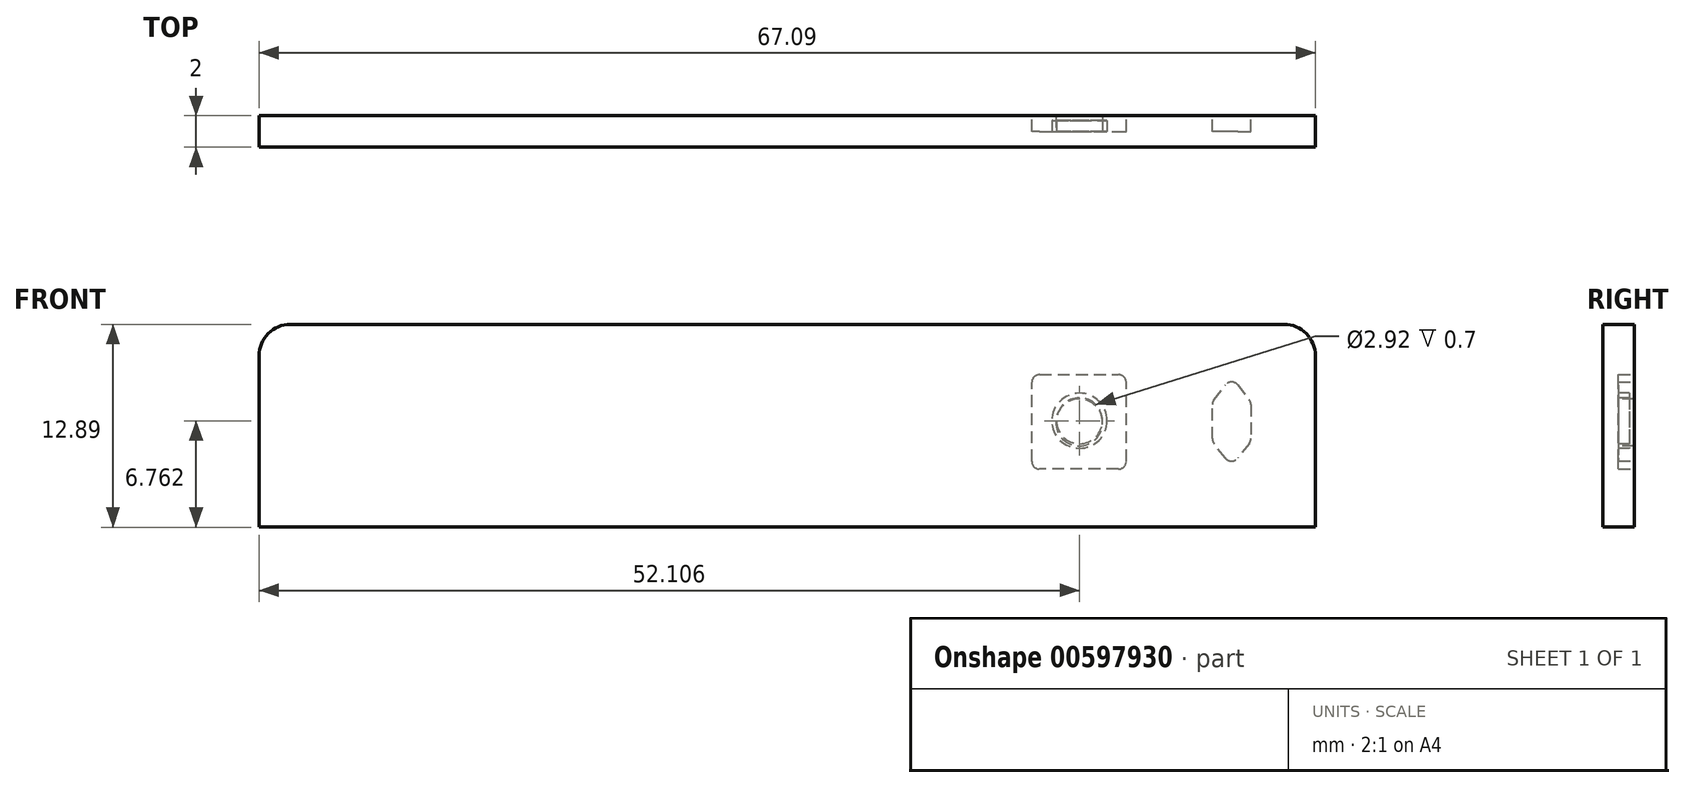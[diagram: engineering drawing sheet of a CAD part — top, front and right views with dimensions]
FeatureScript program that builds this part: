
annotation { "Feature Type Name" : "Feature", "Feature Type Description" : "" }
export const myFeature = defineFeature(function(context is Context, id is Id, definition is map)
    precondition{}
    {
        {
            var Q0;
            Q0=qCreatedBy(makeId("Front.planeOp"),FACE);
            var sketch = newSketch(context, id + "F0", { "sketchPlane" : qUnion([Q0])});
            skLineSegment(sketch, "E0", {"start": v(-68, 133.08) * mm, "end": v(-0.9, 133.08) * mm});
            skLineSegment(sketch, "E1", {"start": v(-0.9, 133.08) * mm, "end": v(-0.9, 143.97) * mm});
            skLineSegment(sketch, "E2", {"start": v(-2.9, 145.97) * mm, "end": v(-66, 145.97) * mm});
            skLineSegment(sketch, "E3", {"start": v(-68, 143.97) * mm, "end": v(-68, 133.08) * mm});
            skPoint(sketch, "E4.visualSharp", {"position": v(-0.9, 145.97) * mm});
            skArc(sketch, "E4.filletArc", {"start": v(-0.9, 143.97) * mm, "mid": v(-1.49, 145.38) * mm, "end": v(-2.9, 145.97) * mm});
            skPoint(sketch, "E5.visualSharp", {"position": v(-68, 145.97) * mm});
            skArc(sketch, "E5.filletArc", {"start": v(-66, 145.97) * mm, "mid": v(-67.4, 145.38) * mm, "end": v(-68, 143.97) * mm});
            skSolve(sketch);
        }
        {
            var Q0;
            Q0=makeQuery(id+"F0.imprint","IMPRINT",FACE,{"disambiguationData":[TD([[makeQuery(id+"F0.imprint","IMPRINT",EDGE,{"derivedFrom":sQuery(id+"F0.wireOp",EDGE,"E0")}),1.0]])]});
            extrude(context, id + "F1", {"entities" : qUnion([Q0]), "oppositeDirection" : true, "depth" : 2 * mm, "offsetDistance" : 25 * mm});
        }
        {
            var Q0;
            Q0=makeQuery(id+"F1.opExtrude","CAP_FACE",FACE,{"disambiguationData":[OSD([sQuery(id+"F0.wireOp",EDGE,"E0"),sQuery(id+"F0.wireOp",EDGE,"E1"),sQuery(id+"F0.wireOp",EDGE,"E2"),sQuery(id+"F0.wireOp",EDGE,"E3"),sQuery(id+"F0.wireOp",EDGE,"E4.filletArc"),sQuery(id+"F0.wireOp",EDGE,"E5.filletArc")])],"isStart":false});
            var sketch = newSketch(context, id + "F2", { "sketchPlane" : qUnion([Q0])});
            skLineSegment(sketch, "E6", {"start": v(13.41, 136.77) * mm, "end": v(18.41, 136.77) * mm});
            skLineSegment(sketch, "E7", {"start": v(18.91, 137.27) * mm, "end": v(18.91, 142.27) * mm});
            skLineSegment(sketch, "E8", {"start": v(18.41, 142.77) * mm, "end": v(13.41, 142.77) * mm});
            skPoint(sketch, "E9.visualSharp", {"position": v(18.91, 142.77) * mm});
            skArc(sketch, "E9.filletArc", {"start": v(18.91, 142.27) * mm, "mid": v(18.77, 142.62) * mm, "end": v(18.41, 142.77) * mm});
            skPoint(sketch, "E10.visualSharp", {"position": v(18.91, 136.77) * mm});
            skArc(sketch, "E10.filletArc", {"start": v(18.41, 136.77) * mm, "mid": v(18.77, 136.92) * mm, "end": v(18.91, 137.27) * mm});
            skPoint(sketch, "E11.visualSharp", {"position": v(12.91, 136.77) * mm});
            skArc(sketch, "E11.filletArc", {"start": v(12.91, 137.27) * mm, "mid": v(13.06, 136.92) * mm, "end": v(13.41, 136.77) * mm});
            skLineSegment(sketch, "E12", {"start": v(12.91, 137.27) * mm, "end": v(12.91, 142.27) * mm});
            skPoint(sketch, "E13.visualSharp", {"position": v(12.91, 142.77) * mm});
            skArc(sketch, "E13.filletArc", {"start": v(13.41, 142.77) * mm, "mid": v(13.06, 142.62) * mm, "end": v(12.91, 142.27) * mm});
            skLineSegment(sketch, "E14", {"start": v(5.83, 142.11) * mm, "end": v(5.1, 141.18) * mm});
            skPoint(sketch, "E14.startSnap0", {"position": v(13.06, 142.62) * mm});
            skLineSegment(sketch, "E15", {"start": v(5, 140.87) * mm, "end": v(5, 138.71) * mm});
            skLineSegment(sketch, "E16", {"start": v(5.1, 138.4) * mm, "end": v(5.83, 137.47) * mm});
            skLineSegment(sketch, "E17", {"start": v(6.62, 137.47) * mm, "end": v(7.34, 138.4) * mm});
            skLineSegment(sketch, "E18", {"start": v(7.45, 138.71) * mm, "end": v(7.45, 140.87) * mm});
            skLineSegment(sketch, "E19", {"start": v(7.34, 141.18) * mm, "end": v(6.62, 142.11) * mm});
            skPoint(sketch, "E20.visualSharp", {"position": v(6.22, 142.62) * mm});
            skArc(sketch, "E20.filletArc", {"start": v(6.62, 142.11) * mm, "mid": v(6.22, 142.3) * mm, "end": v(5.83, 142.11) * mm});
            skPoint(sketch, "E21.visualSharp", {"position": v(5, 141.04) * mm});
            skArc(sketch, "E21.filletArc", {"start": v(5.1, 141.18) * mm, "mid": v(5.03, 141.03) * mm, "end": v(5, 140.87) * mm});
            skPoint(sketch, "E22.visualSharp", {"position": v(7.45, 141.04) * mm});
            skArc(sketch, "E22.filletArc", {"start": v(7.45, 140.87) * mm, "mid": v(7.42, 141.03) * mm, "end": v(7.34, 141.18) * mm});
            skPoint(sketch, "E23.visualSharp", {"position": v(5, 138.54) * mm});
            skArc(sketch, "E23.filletArc", {"start": v(5, 138.71) * mm, "mid": v(5.03, 138.55) * mm, "end": v(5.1, 138.4) * mm});
            skPoint(sketch, "E24.visualSharp", {"position": v(6.22, 136.96) * mm});
            skArc(sketch, "E24.filletArc", {"start": v(5.83, 137.47) * mm, "mid": v(6.22, 137.28) * mm, "end": v(6.62, 137.47) * mm});
            skPoint(sketch, "E25.visualSharp", {"position": v(7.45, 138.54) * mm});
            skArc(sketch, "E25.filletArc", {"start": v(7.34, 138.4) * mm, "mid": v(7.42, 138.55) * mm, "end": v(7.45, 138.71) * mm});
            skSolve(sketch);
        }
        {
            var Q0;
            Q0=makeQuery(id+"F2.imprint","IMPRINT",FACE,{"disambiguationData":[TD([[makeQuery(id+"F2.imprint","IMPRINT",EDGE,{"derivedFrom":sQuery(id+"F2.wireOp",EDGE,"E6")}),1.0]])]});
            var Q1;
            Q1 = qSketchRegion(id + "F2", true);
            extrude(context, id + "F3", {"entities" : qUnion([Q0, Q1]), "operationType" : NewBodyOperationType.REMOVE, "oppositeDirection" : true, "depth" : 1 * mm, "offsetDistance" : 25 * mm});
        }
        {
            var Q0;
            Q0=makeQuery(id+"F3.boolean.opBoolean","COPY",FACE,{"derivedFrom":makeQuery(id+"F3.opExtrude","CAP_FACE",FACE,{"disambiguationData":[OSD([sQuery(id+"F2.wireOp",EDGE,"E6"),sQuery(id+"F2.wireOp",EDGE,"E7"),sQuery(id+"F2.wireOp",EDGE,"E8"),sQuery(id+"F2.wireOp",EDGE,"E9.filletArc"),sQuery(id+"F2.wireOp",EDGE,"E10.filletArc"),sQuery(id+"F2.wireOp",EDGE,"E11.filletArc"),sQuery(id+"F2.wireOp",EDGE,"E12"),sQuery(id+"F2.wireOp",EDGE,"E13.filletArc")])],"isStart":false})});
            var sketch = newSketch(context, id + "F4", { "sketchPlane" : qUnion([Q0])});
            skCircle(sketch, "E26", {"center": v(15.88, 139.84) * mm, "radius": 1.75 * mm});
            skCircle(sketch, "E27", {"center": v(15.88, 139.84) * mm, "radius": 1.46 * mm});
            skSolve(sketch);
        }
        {
            var Q0;
            Q0 = qSketchRegion(id + "F4", true);
            extrude(context, id + "F5", {"entities" : qUnion([Q0]), "depth" : 0.7 * mm, "offsetDistance" : 25 * mm});
        }
        {
            var Q0;
            Q0=makeQuery(id+"F3.boolean.opBoolean","COPY",FACE,{"derivedFrom":makeQuery(id+"F3.opExtrude","CAP_FACE",FACE,{"disambiguationData":[OSD([sQuery(id+"F2.wireOp",EDGE,"E6"),sQuery(id+"F2.wireOp",EDGE,"E7"),sQuery(id+"F2.wireOp",EDGE,"E8"),sQuery(id+"F2.wireOp",EDGE,"E9.filletArc"),sQuery(id+"F2.wireOp",EDGE,"E10.filletArc"),sQuery(id+"F2.wireOp",EDGE,"E11.filletArc"),sQuery(id+"F2.wireOp",EDGE,"E12"),sQuery(id+"F2.wireOp",EDGE,"E13.filletArc")])],"isStart":false})});
            var sketch = newSketch(context, id + "F6", { "sketchPlane" : qUnion([Q0])});
            skCircle(sketch, "E28", {"center": v(15.9, 139.74) * mm, "radius": 1.49 * mm});
            skSolve(sketch);
        }
        {
            var Q0;
            Q0 = qSketchRegion(id + "F6", true);
            extrude(context, id + "F7", {"entities" : qUnion([Q0]), "depth" : 1 * mm, "offsetDistance" : 25 * mm});
        }
    });
